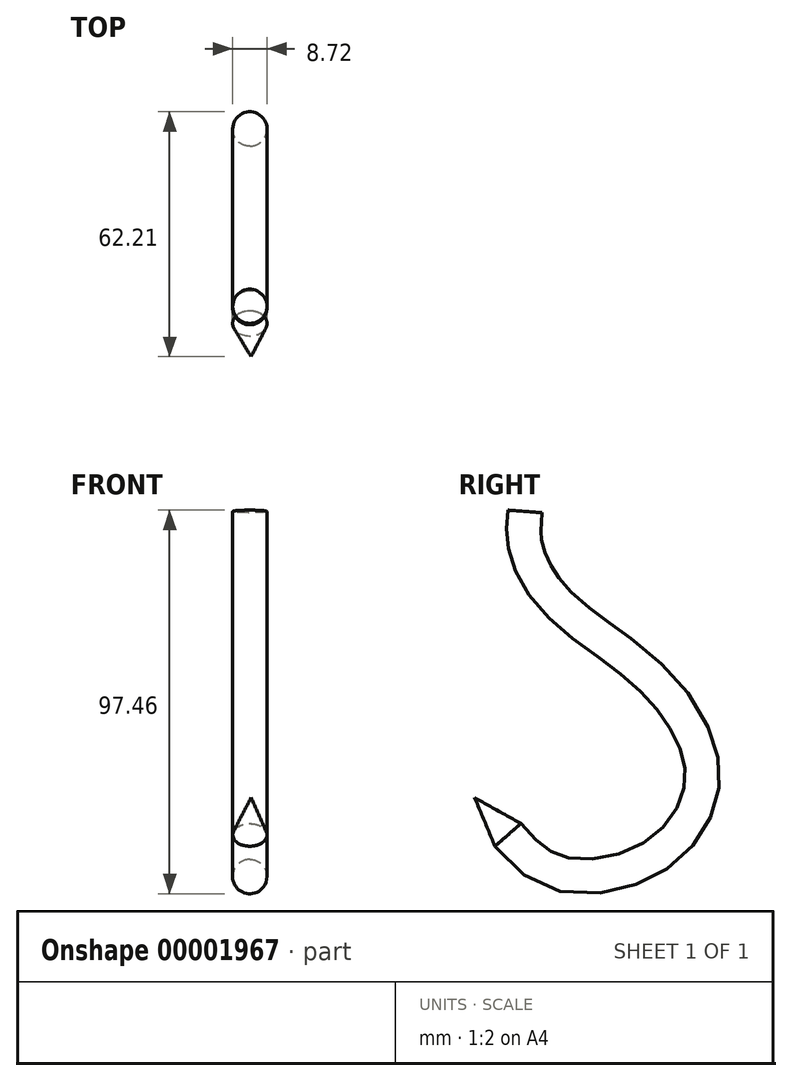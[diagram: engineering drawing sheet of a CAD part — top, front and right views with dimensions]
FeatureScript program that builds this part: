
annotation { "Feature Type Name" : "Feature", "Feature Type Description" : "" }
export const myFeature = defineFeature(function(context is Context, id is Id, definition is map)
    precondition{}
    {
        {
            var Q0;
            Q0=qCreatedBy(makeId("Right.planeOp"),FACE);
            var sketch = newSketch(context, id + "F0", { "sketchPlane" : qUnion([Q0])});
            skFitSpline(sketch, "E0", {"points": [v(0, 0) * mm, v(12.57, -9.69) * mm, v(36.94, -5.66) * mm, v(49.21, 12.18) * mm, v(45, 29.26) * mm, v(30.99, 44.6) * mm, v(11.22, 60.54) * mm, v(4.32, 73.97) * mm, v(4.35, 82.18) * mm], "startDerivative": vector(91.53, -104.6) * mm, "endDerivative": vector(9.7, 128.5) * mm});
            skSolve(sketch);
        }
        {
            var Q0;
            Q0=sQuery(id+"F0.wireOp",EDGE,"E0");
            var Q1;
            Q1=sQuery(id+"F0.wireOp",VERTEX,"E0.0.internal");
            cPlane(context, id + "F1", {"entities" : qUnion([Q0, Q1]), "cplaneType" : CPlaneType.CURVE_POINT, "offset" : 25.4 * mm, "width" : 152.4 * mm, "height" : 152.4 * mm});
        }
        {
            var Q0;
            Q0=qCreatedBy(id+"F1.planeOp",FACE);
            var sketch = newSketch(context, id + "F2", { "sketchPlane" : qUnion([Q0])});
            skCircle(sketch, "E1", {"center": v(0, 0) * mm, "radius": 4.36 * mm});
            skSolve(sketch);
        }
        {
            var Q0;
            Q0=makeQuery(id+"F2.imprint","IMPRINT",FACE,{"disambiguationData":[TD([[makeQuery(id+"F2.imprint","IMPRINT",EDGE,{"derivedFrom":sQuery(id+"F2.wireOp",EDGE,"E1")}),1.0]])]});
            var Q1;
            Q1=sQuery(id+"F0.wireOp",EDGE,"E0");
            sweep(context, id + "F3", {"profiles" : qUnion([Q0]), "path" : qUnion([Q1])});
        }
        {
            var Q0;
            Q0=qCreatedBy(id+"F1.planeOp",FACE);
            cPlane(context, id + "F4", {"entities" : qUnion([Q0]), "cplaneType" : CPlaneType.OFFSET, "offset" : 12.7 * mm, "oppositeDirection" : true, "width" : 152.4 * mm, "height" : 152.4 * mm});
        }
        {
            var Q0;
            Q0=qCreatedBy(id+"F4.planeOp",FACE);
            var sketch = newSketch(context, id + "F5", { "sketchPlane" : qUnion([Q0])});
            skPoint(sketch, "E2", {"position": v(0.32, 0.1) * mm});
            skSolve(sketch);
        }
        {
            var Q0;
            Q0=sQuery(id+"F5.wireOp",VERTEX,"E2");
            var Q1;
            Q1=makeQuery(id+"F2.imprint","IMPRINT",FACE,{"disambiguationData":[TD([[makeQuery(id+"F2.imprint","IMPRINT",EDGE,{"derivedFrom":sQuery(id+"F2.wireOp",EDGE,"E1")}),1.0]])]});
            loft(context, id + "F6", {"sheetProfilesArray" : [{ "sheetProfileEntities" : qUnion([Q0]) }, { "sheetProfileEntities" : qUnion([Q1]) }]});
        }
    });
